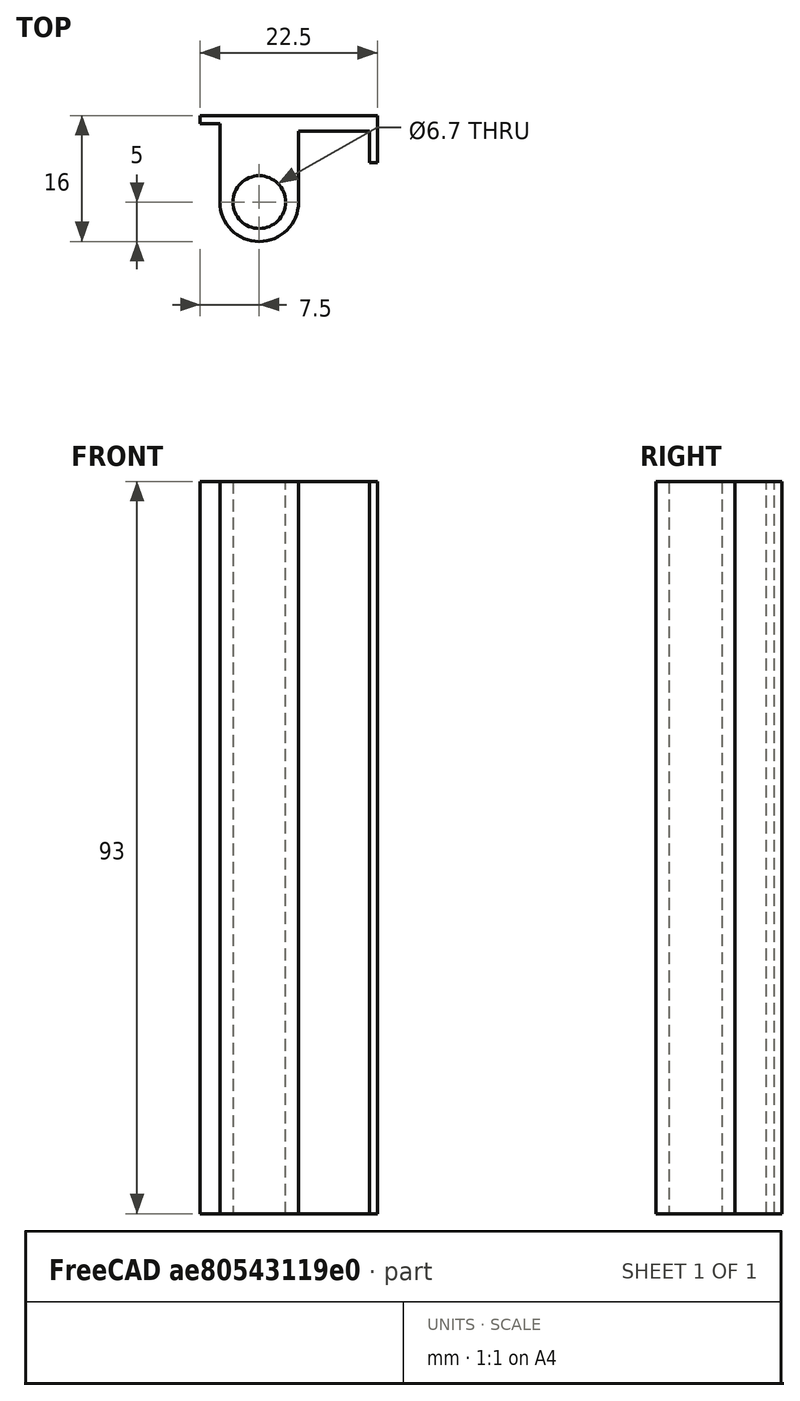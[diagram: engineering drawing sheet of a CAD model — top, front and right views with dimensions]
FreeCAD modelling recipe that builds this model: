
FCSTD DOCUMENT  (FreeCAD 0.18R16110 (Git))
Label: carrier4_6.7_lexm
License: All rights reserved
LicenseURL: http://en.wikipedia.org/wiki/All_rights_reserved
objects: Sketcher::SketchObject×1, PartDesign::Pad×1, PartDesign::Body×1
note: 4 computed .brp shape members not serialized (recipe doc carries the construction recipe); baked Part::Feature solids carry a one-line shape summary decoded from their .brp

FEATURE [Sketcher::SketchObject] Sketch
  MapMode = 5
  Support = -> [XY_Plane]
  sketch-geometry (11):
    g0: LineSegment StartX=20 StartY=1 StartZ=0 EndX=-2.5 EndY=1 EndZ=0
    g1: LineSegment StartX=19 StartY=-1 StartZ=0 EndX=19 EndY=-5 EndZ=0
    g2: LineSegment StartX=19 StartY=-5 StartZ=0 EndX=20 EndY=-5 EndZ=0
    g3: LineSegment StartX=20 StartY=-5 StartZ=0 EndX=20 EndY=1 EndZ=0
    g4: Circle CenterX=5 CenterY=-10 CenterZ=0 NormalX=0 NormalY=0 NormalZ=1 AngleXU=0 Radius=3.35
    g5: ArcOfCircle CenterX=5 CenterY=-10 CenterZ=0 NormalX=0 NormalY=0 NormalZ=1 AngleXU=0 Radius=5 StartAngle=3.14159 EndAngle=6.28319
    g6: LineSegment StartX=0 StartY=-10 StartZ=0 EndX=0 EndY=0 EndZ=0
    g7: LineSegment StartX=10 StartY=-10 StartZ=0 EndX=10 EndY=-1 EndZ=0
    g8: LineSegment StartX=10 StartY=-1 StartZ=0 EndX=19 EndY=-1 EndZ=0
    g9: LineSegment StartX=0 StartY=0 StartZ=0 EndX=-2.5 EndY=0 EndZ=0
    g10: LineSegment StartX=-2.5 StartY=1 StartZ=0 EndX=-2.5 EndY=0 EndZ=0
  constraints (32):
    c: Horizontal(g0)
    c: Coincident(g1,g2)
    c: Coincident(g2,g3)
    c: Coincident(g0,g3)
    c: Vertical(g3)
    c: Vertical(g1)
    c: Horizontal(g2)
    c: DistanceY(g6,g0) = 1
    c: DistanceX(g6,g1) = 19
    c: Distance(g2,g1) = 1
    c: Radius(g5) = 5
    c: Angle(g5) = 3.14159
    c: Vertical(g6)
    c: Vertical(g7)
    c: Horizontal(g8)
    c: Coincident(g7,g8)
    c: Coincident(g5,g7)
    c: Coincident(g5,g6)
    c: Coincident(g4,g5)
    c: Radius(g4) = 3.35
    c: Distance(g4,g0) = 11
    c: Coincident(g0,g10)
    c: Vertical(g10)
    c: Horizontal(g9)
    c: Coincident(g9,g6)
    c: Coincident(g9,g10)
    c: Coincident(g6,g-1)
    c: Distance(g9,g6) = 2.5
    c: Distance(g5,g6) = 10
    c: DistanceY(g3,g3) = 6
    c: Coincident(g8,g1)
    c: Distance(g1,g0) = 2
FEATURE [PartDesign::Pad] Pad
  Length = 93
  Length2 = 100
  Profile = -> Sketch
  Type = 0
FEATURE [PartDesign::Body] Body
  Group = -> [Sketch,Pad]
  Origin = -> Origin
  Tip = -> Pad
